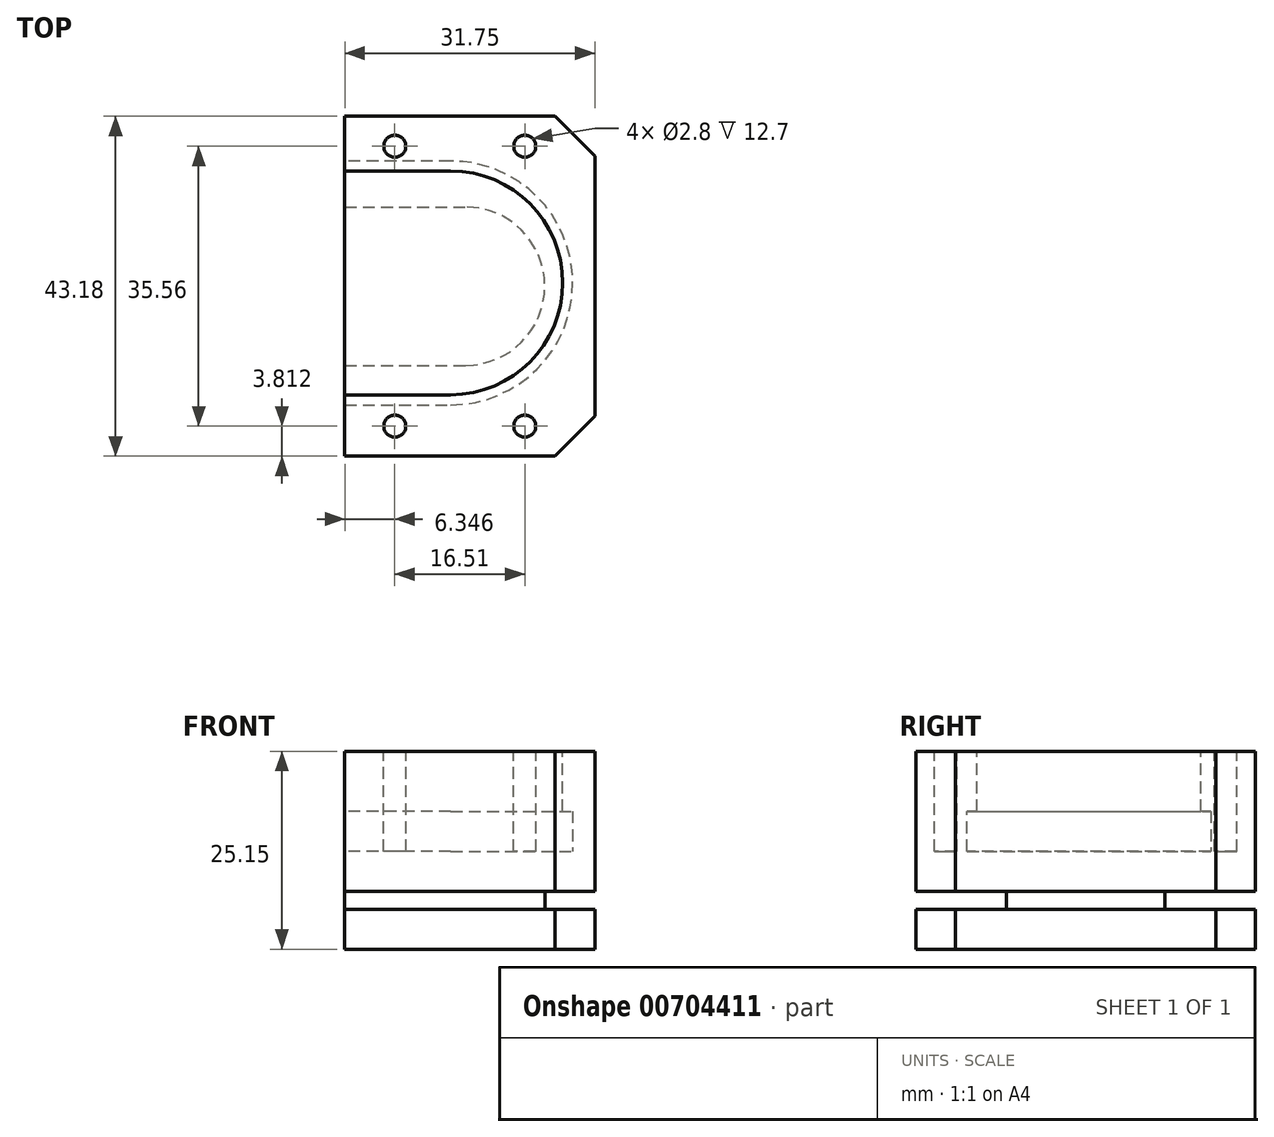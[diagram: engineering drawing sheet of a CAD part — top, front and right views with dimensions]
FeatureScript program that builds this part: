
annotation { "Feature Type Name" : "Feature", "Feature Type Description" : "" }
export const myFeature = defineFeature(function(context is Context, id is Id, definition is map)
    precondition{}
    {
        {
            var Q0;
            Q0=qCreatedBy(makeId("Top.planeOp"),FACE);
            var sketch = newSketch(context, id + "F0", { "sketchPlane" : qUnion([Q0])});
            skLineSegment(sketch, "E0", {"start": v(-17.9, 2.4) * mm, "end": v(-17.9, -10.84) * mm});
            skLineSegment(sketch, "E1", {"start": v(-17.9, -10.84) * mm, "end": v(13.86, -10.84) * mm});
            skLineSegment(sketch, "E2", {"start": v(13.86, -10.84) * mm, "end": v(13.86, 10.75) * mm});
            skLineSegment(sketch, "E3", {"start": v(13.86, 10.75) * mm, "end": v(-17.9, 10.75) * mm, "construction": true});
            skLineSegment(sketch, "E4.MirrorCS", {"start": v(13.86, 32.34) * mm, "end": v(13.86, 10.75) * mm});
            skLineSegment(sketch, "E5.MirrorCS", {"start": v(-17.9, 32.34) * mm, "end": v(13.86, 32.34) * mm});
            skLineSegment(sketch, "E6.MirrorCS", {"start": v(-17.9, 19.11) * mm, "end": v(-17.9, 32.34) * mm});
            skLineSegment(sketch, "E7", {"start": v(-17.9, 19.11) * mm, "end": v(-17.9, 2.4) * mm});
            skSolve(sketch);
        }
        {
            var Q0;
            Q0 = qSketchRegion(id + "F0", true);
            extrude(context, id + "F1", {"entities" : qUnion([Q0]), "depth" : 5.08 * mm, "offsetDistance" : 25.4 * mm});
        }
        {
            var Q0;
            Q0=makeQuery(id+"F1.opExtrude","CAP_FACE",FACE,{"disambiguationData":[OSD([sQuery(id+"F0.wireOp",EDGE,"E0"),sQuery(id+"F0.wireOp",EDGE,"E1"),sQuery(id+"F0.wireOp",EDGE,"E2"),sQuery(id+"F0.wireOp",EDGE,"E4.MirrorCS"),sQuery(id+"F0.wireOp",EDGE,"E5.MirrorCS"),sQuery(id+"F0.wireOp",EDGE,"E6.MirrorCS"),sQuery(id+"F0.wireOp",EDGE,"E7")])],"isStart":false});
            var sketch = newSketch(context, id + "F2", { "sketchPlane" : qUnion([Q0])});
            skLineSegment(sketch, "E8.0.0", {"start": v(-17.9, 32.34) * mm, "end": v(-17.9, -10.84) * mm});
            skLineSegment(sketch, "E8.0.1", {"start": v(-17.9, -10.84) * mm, "end": v(13.86, -10.84) * mm});
            skLineSegment(sketch, "E8.0.2", {"start": v(13.86, -10.84) * mm, "end": v(13.86, 32.34) * mm});
            skLineSegment(sketch, "E8.0.3", {"start": v(13.86, 32.34) * mm, "end": v(-17.9, 32.34) * mm});
            skLineSegment(sketch, "E9", {"start": v(-17.9, 10.75) * mm, "end": v(13.86, 10.75) * mm, "construction": true});
            skLineSegment(sketch, "E10", {"start": v(-17.9, 20.81) * mm, "end": v(-2.55, 20.81) * mm});
            skLineSegment(sketch, "E11.MirrorCS", {"start": v(-17.9, 0.7) * mm, "end": v(-2.55, 0.7) * mm});
            skArc(sketch, "E12", {"start": v(-2.55, 0.7) * mm, "mid": v(7.5, 10.75) * mm, "end": v(-2.55, 20.81) * mm});
            skSolve(sketch);
        }
        {
            var Q0;
            {var subQ0=sQuery(id+"F2.wireOp",EDGE,"E10");Q0=makeQuery(id+"F2.imprint","IMPRINT",FACE,{"disambiguationData":[TD([[makeQuery(id+"F2.imprint","IMPRINT",EDGE,{"derivedFrom":subQ0}),-1.0]])]});}
            extrude(context, id + "F3", {"entities" : qUnion([Q0]), "operationType" : NewBodyOperationType.ADD, "depth" : 2.3 * mm, "offsetDistance" : 25.4 * mm});
        }
        {
            var Q0;
            Q0=makeQuery(id+"F3.opExtrude","CAP_FACE",FACE,{"disambiguationData":[OSD([sQuery(id+"F2.wireOp",EDGE,"E8.0.0"),sQuery(id+"F2.wireOp",EDGE,"E10"),sQuery(id+"F2.wireOp",EDGE,"E11.MirrorCS"),sQuery(id+"F2.wireOp",EDGE,"E12")])],"isStart":false});
            var sketch = newSketch(context, id + "F4", { "sketchPlane" : qUnion([Q0])});
            skLineSegment(sketch, "E13.0.0", {"start": v(-17.9, 32.34) * mm, "end": v(-17.9, 20.81) * mm});
            skLineSegment(sketch, "E13.0.1", {"start": v(-17.9, 20.81) * mm, "end": v(-2.55, 20.81) * mm});
            skArc(sketch, "E13.0.2", {"start": v(-2.55, 20.81) * mm, "mid": v(7.5, 10.75) * mm, "end": v(-2.55, 0.7) * mm});
            skLineSegment(sketch, "E13.0.3", {"start": v(-2.55, 0.7) * mm, "end": v(-17.9, 0.7) * mm});
            skLineSegment(sketch, "E13.0.4", {"start": v(-17.9, 0.7) * mm, "end": v(-17.9, -10.84) * mm});
            skLineSegment(sketch, "E13.0.5", {"start": v(-17.9, -10.84) * mm, "end": v(13.86, -10.84) * mm});
            skLineSegment(sketch, "E13.0.6", {"start": v(13.86, -10.84) * mm, "end": v(13.86, 32.34) * mm});
            skLineSegment(sketch, "E13.0.7", {"start": v(13.86, 32.34) * mm, "end": v(-17.9, 32.34) * mm});
            skLineSegment(sketch, "E14.0", {"start": v(-17.9, 0.7) * mm, "end": v(-17.9, 20.81) * mm});
            skSolve(sketch);
        }
        {
            var Q0;
            Q0=makeQuery(id+"F4.imprint","IMPRINT",FACE,{"disambiguationData":[TD([[makeQuery(id+"F4.imprint","IMPRINT",EDGE,{"derivedFrom":sQuery(id+"F4.wireOp",EDGE,"E13.0.1")}),-1.0]])]});
            var Q1;
            Q1=makeQuery(id+"F4.imprint","IMPRINT",FACE,{"disambiguationData":[TD([[makeQuery(id+"F4.imprint","IMPRINT",EDGE,{"derivedFrom":sQuery(id+"F4.wireOp",EDGE,"E13.0.0")}),1.0]])]});
            extrude(context, id + "F5", {"entities" : qUnion([Q0, Q1]), "operationType" : NewBodyOperationType.ADD, "depth" : 17.78 * mm, "offsetDistance" : 25.4 * mm});
        }
        {
            var Q0;
            Q0=makeQuery(id+"F5.opExtrude","SWEPT_EDGE",EDGE,{"disambiguationData":[OSD([sQuery(id+"F4.wireOp",EDGE,"E13.0.5"),sQuery(id+"F4.wireOp",EDGE,"E13.0.6")])]});
            var Q1;
            Q1=makeQuery(id+"F1.opExtrude","SWEPT_EDGE",EDGE,{"disambiguationData":[OSD([sQuery(id+"F0.wireOp",EDGE,"E1"),sQuery(id+"F0.wireOp",EDGE,"E2")])]});
            var Q2;
            Q2=makeQuery(id+"F5.opExtrude","SWEPT_EDGE",EDGE,{"disambiguationData":[OSD([sQuery(id+"F4.wireOp",EDGE,"E13.0.6"),sQuery(id+"F4.wireOp",EDGE,"E13.0.7")])]});
            var Q3;
            Q3=makeQuery(id+"F1.opExtrude","SWEPT_EDGE",EDGE,{"disambiguationData":[OSD([sQuery(id+"F0.wireOp",EDGE,"E4.MirrorCS"),sQuery(id+"F0.wireOp",EDGE,"E5.MirrorCS")])]});
            chamfer(context, id + "F6", {"entities" : qUnion([Q0, Q1, Q2, Q3]), "width" : 5.08 * mm, "tangentPropagation" : true});
        }
        {
            var Q0;
            Q0=makeQuery(id+"F5.opExtrude","CAP_FACE",FACE,{"disambiguationData":[OSD([sQuery(id+"F4.wireOp",EDGE,"E13.0.0"),sQuery(id+"F4.wireOp",EDGE,"E13.0.4"),sQuery(id+"F4.wireOp",EDGE,"E13.0.5"),sQuery(id+"F4.wireOp",EDGE,"E13.0.6"),sQuery(id+"F4.wireOp",EDGE,"E13.0.7"),sQuery(id+"F4.wireOp",EDGE,"E14.0")])],"isStart":false});
            var sketch = newSketch(context, id + "F7", { "sketchPlane" : qUnion([Q0])});
            skLineSegment(sketch, "E15", {"start": v(-17.9, 10.75) * mm, "end": v(13.86, 10.75) * mm, "construction": true});
            skLineSegment(sketch, "E16.0", {"start": v(-17.9, 32.34) * mm, "end": v(-17.9, -10.84) * mm});
            skCircle(sketch, "E17", {"center": v(-11.54, 28.53) * mm, "radius": 1.4 * mm});
            skCircle(sketch, "E18", {"center": v(4.97, 28.53) * mm, "radius": 1.4 * mm});
            skCircle(sketch, "E19.MirrorC", {"center": v(-11.54, -7.03) * mm, "radius": 1.4 * mm});
            skCircle(sketch, "E20.MirrorC", {"center": v(4.97, -7.03) * mm, "radius": 1.4 * mm});
            skLineSegment(sketch, "E21", {"start": v(-17.9, 25.4) * mm, "end": v(-17.9, -3.05) * mm});
            skLineSegment(sketch, "E22", {"start": v(-17.9, 25.4) * mm, "end": v(-4.44, 25.4) * mm});
            skArc(sketch, "E23", {"start": v(-4.44, -3.05) * mm, "mid": v(9.78, 11.17) * mm, "end": v(-4.44, 25.4) * mm});
            skLineSegment(sketch, "E24", {"start": v(-17.9, -3.05) * mm, "end": v(-4.44, -3.05) * mm});
            skSolve(sketch);
        }
        {
            var Q0;
            Q0 = qSketchRegion(id + "F7", true);
            extrude(context, id + "F8", {"entities" : qUnion([Q0]), "operationType" : NewBodyOperationType.REMOVE, "oppositeDirection" : true, "depth" : 12.7 * mm, "offsetDistance" : 25.4 * mm});
        }
        {
            var Q0;
            Q0=makeQuery(id+"F8.boolean.opBoolean","COPY",FACE,{"derivedFrom":makeQuery(id+"F8.opExtrude","CAP_FACE",FACE,{"disambiguationData":[OSD([sQuery(id+"F7.wireOp",EDGE,"E21"),sQuery(id+"F7.wireOp",EDGE,"E22"),sQuery(id+"F7.wireOp",EDGE,"E23"),sQuery(id+"F7.wireOp",EDGE,"E24")])],"isStart":false})});
            var sketch = newSketch(context, id + "F9", { "sketchPlane" : qUnion([Q0])});
            skLineSegment(sketch, "E25.0", {"start": v(-19.16, 26.66) * mm, "end": v(-19.16, -4.32) * mm});
            skLineSegment(sketch, "E25.1", {"start": v(-4.44, 26.66) * mm, "end": v(-19.16, 26.66) * mm});
            skArc(sketch, "E25.2", {"start": v(-4.44, -4.32) * mm, "mid": v(11.05, 11.17) * mm, "end": v(-4.44, 26.66) * mm});
            skLineSegment(sketch, "E25.3", {"start": v(-19.16, -4.32) * mm, "end": v(-4.44, -4.32) * mm});
            skSolve(sketch);
        }
        {
            var Q0;
            Q0 = qSketchRegion(id + "F9", true);
            extrude(context, id + "F10", {"entities" : qUnion([Q0]), "operationType" : NewBodyOperationType.REMOVE, "depth" : 5.08 * mm, "offsetDistance" : 25.4 * mm});
        }
    });
